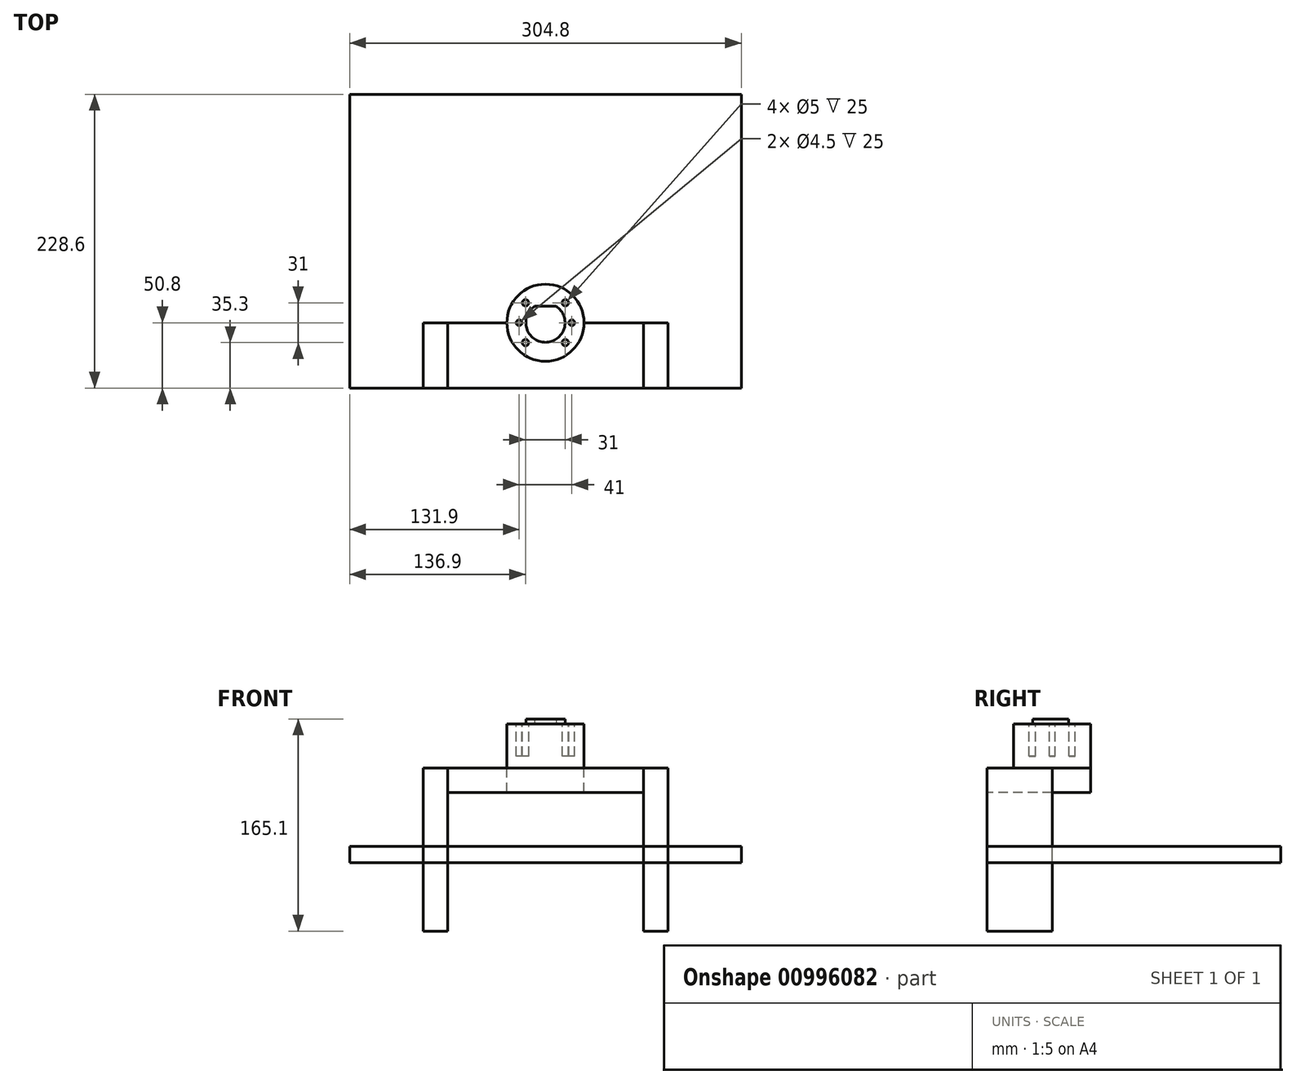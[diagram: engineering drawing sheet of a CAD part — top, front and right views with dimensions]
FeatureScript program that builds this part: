
annotation { "Feature Type Name" : "Feature", "Feature Type Description" : "" }
export const myFeature = defineFeature(function(context is Context, id is Id, definition is map)
    precondition{}
    {
        {
            var Q0;
            Q0=qCreatedBy(makeId("Top.planeOp"),FACE);
            var sketch = newSketch(context, id + "F0", { "sketchPlane" : qUnion([Q0])});
            skCircle(sketch, "E0", {"center": v(0, 0) * mm, "radius": 30 * mm});
            skSolve(sketch);
        }
        {
            var Q0;
            Q0=qSketchRegion(id+"F0",true);
            extrude(context, id + "F1", {"entities" : qUnion([Q0]), "oppositeDirection" : true, "depth" : 34.1 * mm, "offsetDistance" : 25 * mm});
        }
        {
            var Q0;
            Q0=makeQuery(id+"F1.opExtrude","CAP_FACE",FACE,{"disambiguationData":[OSD([sQuery(id+"F0.wireOp",EDGE,"E0")])],"isStart":true});
            var sketch = newSketch(context, id + "F2", { "sketchPlane" : qUnion([Q0])});
            skArc(sketch, "E1", {"start": v(-8.37, 12.75) * mm, "mid": v(0, -15.25) * mm, "end": v(8.37, 12.75) * mm});
            skLineSegment(sketch, "E2", {"start": v(-8.37, 12.75) * mm, "end": v(8.37, 12.75) * mm});
            skPoint(sketch, "E3.orphan", {"position": v(21.18, 12.75) * mm});
            skSolve(sketch);
        }
        {
            var Q0;
            Q0=qSketchRegion(id+"F2",true);
            extrude(context, id + "F3", {"entities" : qUnion([Q0]), "operationType" : NewBodyOperationType.ADD, "depth" : 4 * mm, "offsetDistance" : 25 * mm});
        }
        {
            var Q0;
            Q0=makeQuery(id+"F1.opExtrude","CAP_FACE",FACE,{"disambiguationData":[OSD([sQuery(id+"F0.wireOp",EDGE,"E0")])],"isStart":true});
            var sketch = newSketch(context, id + "F4", { "sketchPlane" : qUnion([Q0])});
            skLineSegment(sketch, "E4.bottom", {"start": v(15.5, 15.5) * mm, "end": v(-15.5, 15.5) * mm, "construction": true});
            skLineSegment(sketch, "E4.top", {"start": v(15.5, -15.5) * mm, "end": v(-15.5, -15.5) * mm, "construction": true});
            skLineSegment(sketch, "E4.left", {"start": v(15.5, 15.5) * mm, "end": v(15.5, -15.5) * mm, "construction": true});
            skLineSegment(sketch, "E4.right", {"start": v(-15.5, 15.5) * mm, "end": v(-15.5, -15.5) * mm, "construction": true});
            skPoint(sketch, "E4.middle", {"position": v(0, 0) * mm});
            skCircle(sketch, "E5", {"center": v(15.5, 15.5) * mm, "radius": 2.5 * mm});
            skCircle(sketch, "E6", {"center": v(-15.5, 15.5) * mm, "radius": 2.5 * mm});
            skCircle(sketch, "E7", {"center": v(-15.5, -15.5) * mm, "radius": 2.5 * mm});
            skCircle(sketch, "E8", {"center": v(15.5, -15.5) * mm, "radius": 2.5 * mm});
            skLineSegment(sketch, "E9", {"start": v(-20.5, 0) * mm, "end": v(20.5, 0) * mm, "construction": true});
            skCircle(sketch, "E10", {"center": v(-20.5, 0) * mm, "radius": 2.25 * mm});
            skCircle(sketch, "E11", {"center": v(20.5, 0) * mm, "radius": 2.25 * mm});
            skSolve(sketch);
        }
        {
            var Q0;
            Q0=qSketchRegion(id+"F4",true);
            extrude(context, id + "F5", {"entities" : qUnion([Q0]), "operationType" : NewBodyOperationType.REMOVE, "oppositeDirection" : true, "depth" : 25 * mm, "offsetDistance" : 25 * mm});
        }
        {
            var Q0;
            Q0=makeQuery(id+"F1.opExtrude","CAP_FACE",FACE,{"disambiguationData":[OSD([sQuery(id+"F0.wireOp",EDGE,"E0")])],"isStart":false});
            var sketch = newSketch(context, id + "F6", { "sketchPlane" : qUnion([Q0])});
            skLineSegment(sketch, "E12.bottom", {"start": v(-76.2, 0) * mm, "end": v(76.2, 0) * mm});
            skLineSegment(sketch, "E12.top", {"start": v(-76.2, 50.8) * mm, "end": v(76.2, 50.8) * mm});
            skLineSegment(sketch, "E12.left", {"start": v(-76.2, 0) * mm, "end": v(-76.2, 50.8) * mm});
            skLineSegment(sketch, "E12.right", {"start": v(76.2, 0) * mm, "end": v(76.2, 50.8) * mm});
            skCircle(sketch, "E13", {"center": v(0, 0) * mm, "radius": 30 * mm});
            skSolve(sketch);
        }
        {
            var Q0;
            Q0 = qSketchRegion(id + "F6", true);
            extrude(context, id + "F7", {"entities" : qUnion([Q0]), "depth" : 19.05 * mm, "offsetDistance" : 25 * mm});
        }
        {
            var Q0;
            Q0=makeQuery(id+"F7.opExtrude","SWEPT_FACE",FACE,{"disambiguationData":[OSD([sQuery(id+"F6.wireOp",EDGE,"E12.right")])]});
            var sketch = newSketch(context, id + "F8", { "sketchPlane" : qUnion([Q0])});
            skLineSegment(sketch, "E14.bottom", {"start": v(-50.8, -34.1) * mm, "end": v(0, -34.1) * mm});
            skLineSegment(sketch, "E14.top", {"start": v(-50.8, -161.1) * mm, "end": v(0, -161.1) * mm});
            skLineSegment(sketch, "E14.left", {"start": v(-50.8, -34.1) * mm, "end": v(-50.8, -161.1) * mm});
            skLineSegment(sketch, "E14.right", {"start": v(0, -34.1) * mm, "end": v(0, -161.1) * mm});
            skSolve(sketch);
        }
        {
            var Q0;
            Q0 = qSketchRegion(id + "F8", true);
            extrude(context, id + "F9", {"entities" : qUnion([Q0]), "depth" : 19.05 * mm, "offsetDistance" : 25 * mm});
        }
        {
            var Q0;
            Q0=makeQuery(id+"F7.opExtrude","SWEPT_FACE",FACE,{"disambiguationData":[OSD([sQuery(id+"F6.wireOp",EDGE,"E12.left")])]});
            var sketch = newSketch(context, id + "F10", { "sketchPlane" : qUnion([Q0])});
            skLineSegment(sketch, "E15.bottom", {"start": v(50.8, -34.1) * mm, "end": v(0, -34.1) * mm});
            skLineSegment(sketch, "E15.top", {"start": v(50.8, -161.1) * mm, "end": v(0, -161.1) * mm});
            skLineSegment(sketch, "E15.left", {"start": v(50.8, -34.1) * mm, "end": v(50.8, -161.1) * mm});
            skLineSegment(sketch, "E15.right", {"start": v(0, -34.1) * mm, "end": v(0, -161.1) * mm});
            skSolve(sketch);
        }
        {
            var Q0;
            Q0 = qSketchRegion(id + "F10", true);
            extrude(context, id + "F11", {"entities" : qUnion([Q0]), "depth" : 19.05 * mm, "offsetDistance" : 25 * mm});
        }
        {
            var Q0;
            Q0=qCreatedBy(makeId("Top.planeOp"),FACE);
            cPlane(context, id + "F12", {"entities" : qUnion([Q0]), "cplaneType" : CPlaneType.OFFSET, "offset" : 95.25 * mm, "oppositeDirection" : true, "width" : 150 * mm, "height" : 150 * mm});
        }
        {
            var Q0;
            Q0=qCreatedBy(id+"F12.planeOp",FACE);
            var sketch = newSketch(context, id + "F13", { "sketchPlane" : qUnion([Q0])});
            skLineSegment(sketch, "E16.bottom", {"start": v(-152.4, -50.8) * mm, "end": v(152.4, -50.8) * mm});
            skLineSegment(sketch, "E16.top", {"start": v(-152.4, 177.8) * mm, "end": v(152.4, 177.8) * mm});
            skLineSegment(sketch, "E16.left", {"start": v(-152.4, -50.8) * mm, "end": v(-152.4, 177.8) * mm});
            skLineSegment(sketch, "E16.right", {"start": v(152.4, -50.8) * mm, "end": v(152.4, 177.8) * mm});
            skSolve(sketch);
        }
        {
            var Q0;
            Q0 = qSketchRegion(id + "F13", true);
            extrude(context, id + "F14", {"entities" : qUnion([Q0]), "oppositeDirection" : true, "depth" : 12.7 * mm, "offsetDistance" : 25.4 * mm});
        }
    });
